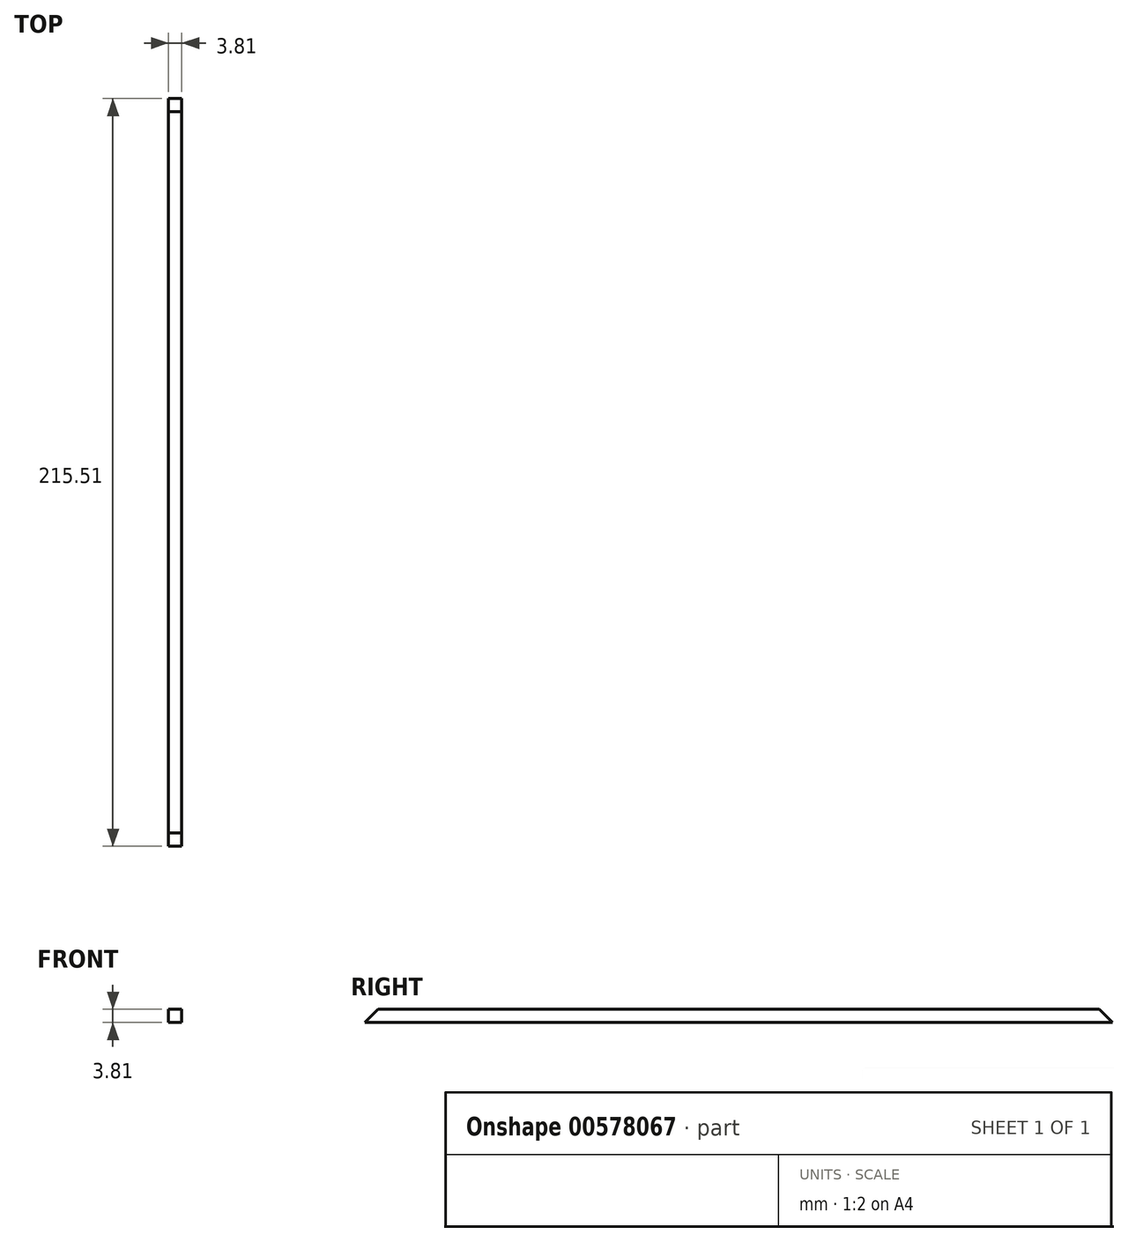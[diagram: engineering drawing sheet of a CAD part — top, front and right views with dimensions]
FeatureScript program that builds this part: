
annotation { "Feature Type Name" : "Feature", "Feature Type Description" : "" }
export const myFeature = defineFeature(function(context is Context, id is Id, definition is map)
    precondition{}
    {
        {
            var Q0;
            Q0=qCreatedBy(makeId("Top.planeOp"),FACE);
            var sketch = newSketch(context, id + "F0", { "sketchPlane" : qUnion([Q0])});
            skLineSegment(sketch, "E0.bottom", {"start": v(86.87, 214.3) * mm, "end": v(90.68, 214.3) * mm});
            skLineSegment(sketch, "E0.top", {"start": v(86.87, -1.22) * mm, "end": v(90.68, -1.22) * mm});
            skLineSegment(sketch, "E0.left", {"start": v(86.87, 214.3) * mm, "end": v(86.87, -1.22) * mm});
            skLineSegment(sketch, "E0.right", {"start": v(90.68, 214.3) * mm, "end": v(90.68, -1.22) * mm});
            skSolve(sketch);
        }
        {
            var Q0;
            Q0 = qSketchRegion(id + "F0", true);
            extrude(context, id + "F1", {"entities" : qUnion([Q0]), "depth" : 3.8 * mm, "offsetDistance" : 25.4 * mm});
        }
        {
            var Q0;
            Q0=makeQuery(id+"F1.opExtrude","CAP_EDGE",EDGE,{"disambiguationData":[OSD([sQuery(id+"F0.wireOp",EDGE,"E0.top")])],"isStart":false});
            chamfer(context, id + "F2", {"entities" : qUnion([Q0]), "width" : 3.8 * mm, "tangentPropagation" : true});
        }
        {
            var Q0;
            Q0=makeQuery(id+"F1.opExtrude","CAP_EDGE",EDGE,{"disambiguationData":[OSD([sQuery(id+"F0.wireOp",EDGE,"E0.bottom")])],"isStart":false});
            chamfer(context, id + "F3", {"entities" : qUnion([Q0]), "width" : 3.8 * mm, "tangentPropagation" : true});
        }
    });
